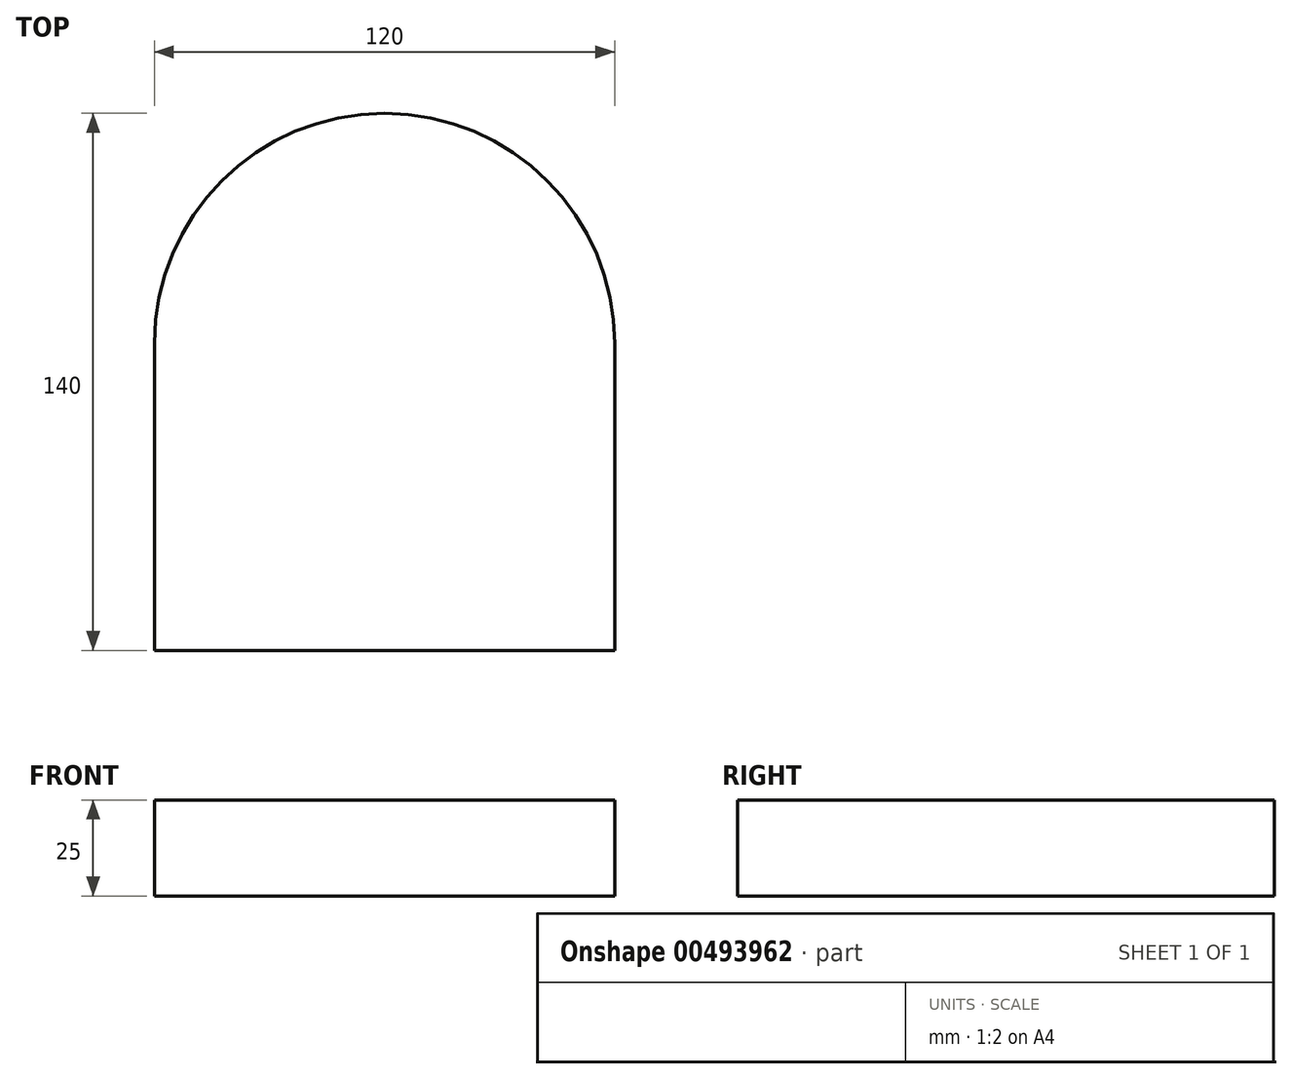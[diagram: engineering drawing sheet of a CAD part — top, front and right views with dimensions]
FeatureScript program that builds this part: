
annotation { "Feature Type Name" : "Feature", "Feature Type Description" : "" }
export const myFeature = defineFeature(function(context is Context, id is Id, definition is map)
    precondition{}
    {
        {
            var Q0;
            Q0=qCreatedBy(makeId("Top.planeOp"),FACE);
            var sketch = newSketch(context, id + "F0", { "sketchPlane" : qUnion([Q0])});
            skArc(sketch, "E0", {"start": v(-60, 0) * mm, "mid": v(0, 60) * mm, "end": v(60, 0) * mm});
            skLineSegment(sketch, "E1.bottom", {"start": v(-60, 0) * mm, "end": v(60, 0) * mm, "construction": true});
            skLineSegment(sketch, "E1.top", {"start": v(-60, -80) * mm, "end": v(60, -80) * mm});
            skLineSegment(sketch, "E1.left", {"start": v(-60, 0) * mm, "end": v(-60, -80) * mm});
            skLineSegment(sketch, "E1.right", {"start": v(60, 0) * mm, "end": v(60, -80) * mm});
            skSolve(sketch);
        }
        {
            var Q0;
            Q0 = qSketchRegion(id + "F0", true);
            extrude(context, id + "F1", {"entities" : qUnion([Q0]), "depth" : 25 * mm});
        }
    });
